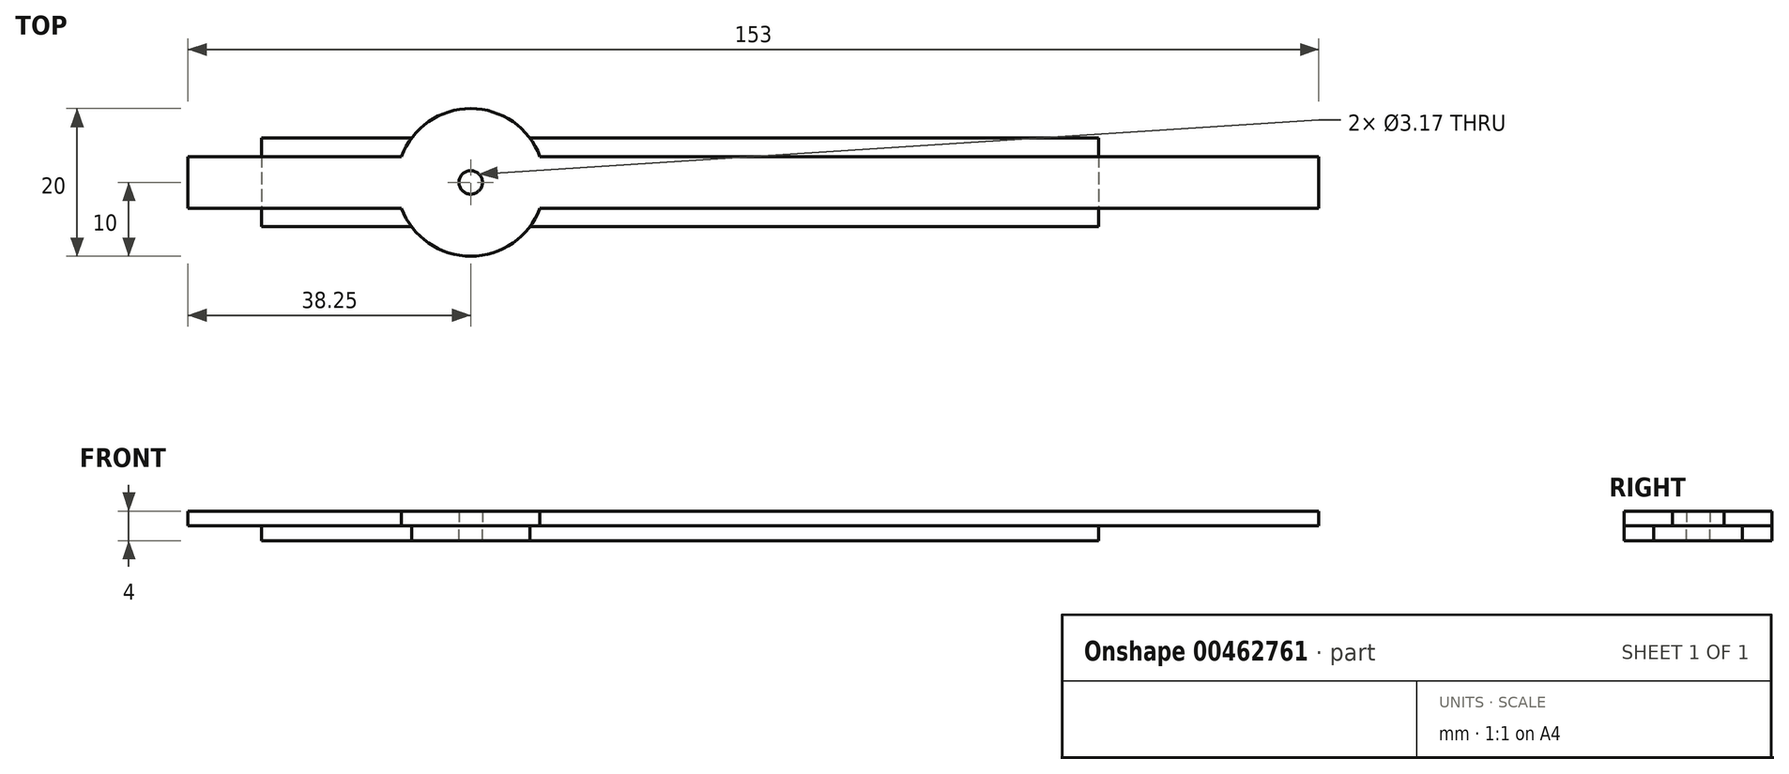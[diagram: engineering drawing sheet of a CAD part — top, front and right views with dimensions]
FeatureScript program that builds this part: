
annotation { "Feature Type Name" : "Feature", "Feature Type Description" : "" }
export const myFeature = defineFeature(function(context is Context, id is Id, definition is map)
    precondition{}
    {
        {
            var Q0;
            Q0=qCreatedBy(makeId("Top.planeOp"),FACE);
            var sketch = newSketch(context, id + "F0", { "sketchPlane" : qUnion([Q0])});
            skCircle(sketch, "E0", {"center": v(0, 0) * mm, "radius": 1.59 * mm});
            skLineSegment(sketch, "E1.bottom", {"start": v(-38.25, 3.5) * mm, "end": v(114.75, 3.5) * mm});
            skLineSegment(sketch, "E1.top", {"start": v(-38.25, -3.5) * mm, "end": v(114.75, -3.5) * mm});
            skLineSegment(sketch, "E1.left", {"start": v(-38.25, 3.5) * mm, "end": v(-38.25, -3.5) * mm});
            skLineSegment(sketch, "E1.right", {"start": v(114.75, 3.5) * mm, "end": v(114.75, -3.5) * mm});
            skCircle(sketch, "E2", {"center": v(0, 0) * mm, "radius": 10 * mm});
            skSolve(sketch);
        }
        {
            var Q0;
            Q0 = qSketchRegion(id + "F0", true);
            extrude(context, id + "F1", {"entities" : qUnion([Q0]), "depth" : 2 * mm});
        }
        {
            var Q0;
            Q0=qCreatedBy(makeId("Top.planeOp"),FACE);
            var sketch = newSketch(context, id + "F2", { "sketchPlane" : qUnion([Q0])});
            skCircle(sketch, "E3", {"center": v(0, 0) * mm, "radius": 1.59 * mm});
            skLineSegment(sketch, "E4.bottom", {"start": v(-28.33, 6) * mm, "end": v(85, 6) * mm});
            skLineSegment(sketch, "E4.top", {"start": v(-28.33, -6) * mm, "end": v(85, -6) * mm});
            skLineSegment(sketch, "E4.left", {"start": v(-28.33, 6) * mm, "end": v(-28.33, -6) * mm});
            skLineSegment(sketch, "E4.right", {"start": v(85, 6) * mm, "end": v(85, -6) * mm});
            skCircle(sketch, "E5", {"center": v(0, 0) * mm, "radius": 10 * mm});
            skSolve(sketch);
        }
        {
            var Q0;
            Q0 = qSketchRegion(id + "F2", true);
            extrude(context, id + "F3", {"entities" : qUnion([Q0]), "oppositeDirection" : true, "depth" : 2 * mm});
        }
    });
